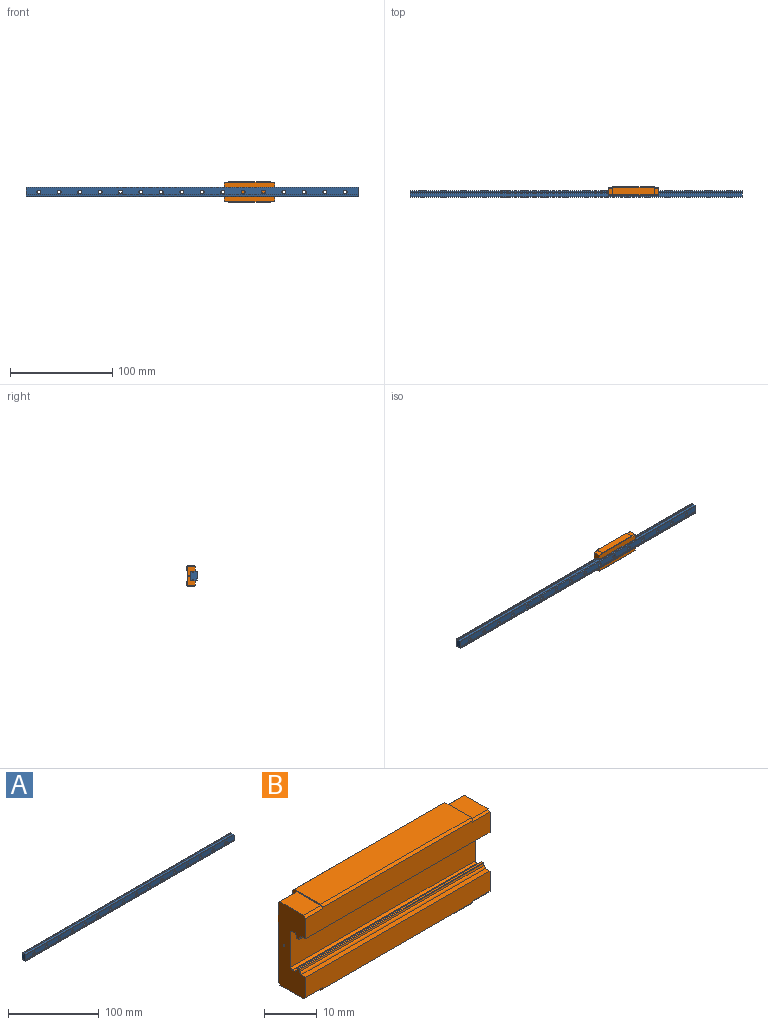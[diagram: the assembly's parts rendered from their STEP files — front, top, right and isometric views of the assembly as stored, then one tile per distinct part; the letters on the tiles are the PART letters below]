
ASSEMBLY  parts=2 mates=1
PART A: 92 faces, bbox 325x6x9 mm
  f0: cylinder r=1mm len=325mm, axis (-1,0,0), area 211.8mm2, adj f1,f25,f26,f27
  f1: plane 325x0.72mm, normal (0,0,1), area 235.4mm2, adj f0,f2,f26,f27
  f2: cylinder r=0.79mm len=325mm, axis (-1,0,0), area 217.9mm2, adj f1,f3,f26,f27
  f3: plane 325x0.45mm, normal (0,-0.98,0.18), area 148.1mm2, adj f2,f4,f26,f27
  f4: cylinder r=0.4mm len=325mm, axis (-1,0,0), area 61.9mm2, adj f3,f5,f26,f27
  f5: plane 325x0.35mm, normal (0,0,1), area 113.3mm2, adj f4,f6,f26,f27
  f6: cylinder r=0.4mm len=325mm, axis (-1,0,0), area 61.9mm2, adj f5,f7,f26,f27
  f7: plane 325x0.45mm, normal (0,0.98,0.18), area 148.1mm2, adj f6,f8,f26,f27
  f8: cylinder r=0.79mm len=325mm, axis (-1,0,0), area 217.9mm2, adj f7,f9,f26,f27
  f9: plane 325x2.72mm, normal (0,0,1), area 885.4mm2, adj f8,f10,f26,f27
  f10: plane 325x0.5mm, normal (0,-0.71,0.71), area 229.8mm2, adj f9,f11,f26,f27
  f11: plane 325x6.1mm, normal (0,-1,0), area 1791.4mm2, adj f10,f12,f26,f27,f31,f35,f39,f43
  f12: cylinder r=0.5mm len=325mm, axis (-1,0,0), area 301.4mm2, adj f11,f13,f26,f27
  f13: plane 325x1.1mm, normal (0,-1,0), area 357.5mm2, adj f12,f14,f26,f27
  f14: plane 325x0.5mm, normal (0,-0.71,-0.71), area 229.8mm2, adj f13,f15,f26,f27
  f15: plane 325x2.72mm, normal (0,0,-1), area 885.4mm2, adj f14,f16,f26,f27
  f16: cylinder r=0.79mm len=325mm, axis (-1,0,0), area 217.9mm2, adj f15,f17,f26,f27
  f17: plane 325x0.45mm, normal (0,0.98,-0.18), area 148.1mm2, adj f16,f18,f26,f27
  f18: cylinder r=0.4mm len=325mm, axis (-1,0,0), area 61.9mm2, adj f17,f19,f26,f27
  f19: plane 325x0.35mm, normal (0,0,-1), area 113.3mm2, adj f18,f20,f26,f27
  f20: cylinder r=0.4mm len=325mm, axis (-1,0,0), area 61.9mm2, adj f19,f21,f26,f27
  f21: plane 325x0.45mm, normal (0,-0.98,-0.18), area 148.1mm2, adj f20,f22,f26,f27
  f22: cylinder r=0.79mm len=325mm, axis (-1,0,0), area 217.9mm2, adj f21,f23,f26,f27
  f23: plane 325x0.72mm, normal (0,0,-1), area 235.4mm2, adj f22,f24,f26,f27
  f24: cylinder r=1mm len=325mm, axis (-1,0,0), area 211.8mm2, adj f23,f25,f26,f27
  f25: plane 325x8.2mm, normal (0,1,0), area 2212.6mm2, adj f0,f24,f26,f27,f28,f32,f36,f40
  f26: plane 9x6mm, normal (1,0,0), area 51.3mm2, adj f0,f1,f2,f3,f4,f5,f6,f7
  f27: plane 9x6mm, normal (-1,0,0), area 51.3mm2, adj f0,f1,f2,f3,f4,f5,f6,f7
  f28: cylinder r=3mm len=6mm, axis (0,-1,0), area 66mm2, adj f25,f29
  f29: plane 6x6mm, normal (0,1,0), area 18.7mm2, adj f28,f30
  f30: cylinder r=1.75mm len=3.5mm, axis (0,-1,0), area 25.3mm2, adj f29,f31
  f31: cone r=1.75mm half-angle=45deg, axis (0,-1,0), area 3.3mm2, adj f11,f30
  f32: cylinder r=3mm len=6mm, axis (0,-1,0), area 66mm2, adj f25,f33
  f33: plane 6x6mm, normal (0,1,0), area 18.7mm2, adj f32,f34
  f34: cylinder r=1.75mm len=3.5mm, axis (0,-1,0), area 25.3mm2, adj f33,f35
  f35: cone r=1.75mm half-angle=45deg, axis (0,-1,0), area 3.3mm2, adj f11,f34
  f36: cylinder r=3mm len=6mm, axis (0,-1,0), area 66mm2, adj f25,f37
  f37: plane 6x6mm, normal (0,1,0), area 18.7mm2, adj f36,f38
  f38: cylinder r=1.75mm len=3.5mm, axis (0,-1,0), area 25.3mm2, adj f37,f39
  f39: cone r=1.75mm half-angle=45deg, axis (0,-1,0), area 3.3mm2, adj f11,f38
  f40: cylinder r=3mm len=6mm, axis (0,-1,0), area 66mm2, adj f25,f41
  f41: plane 6x6mm, normal (0,1,0), area 18.7mm2, adj f40,f42
  f42: cylinder r=1.75mm len=3.5mm, axis (0,-1,0), area 25.3mm2, adj f41,f43
  f43: cone r=1.75mm half-angle=45deg, axis (0,-1,0), area 3.3mm2, adj f11,f42
  f44: cylinder r=3mm len=6mm, axis (0,-1,0), area 66mm2, adj f25,f45
  f45: plane 6x6mm, normal (0,1,0), area 18.7mm2, adj f44,f46
  f46: cylinder r=1.75mm len=3.5mm, axis (0,-1,0), area 25.3mm2, adj f45,f47
  f47: cone r=1.75mm half-angle=45deg, axis (0,-1,0), area 3.3mm2, adj f11,f46
  f48: cylinder r=3mm len=6mm, axis (0,-1,0), area 66mm2, adj f25,f49
  f49: plane 6x6mm, normal (0,1,0), area 18.7mm2, adj f48,f50
  f50: cylinder r=1.75mm len=3.5mm, axis (0,-1,0), area 25.3mm2, adj f49,f51
  f51: cone r=1.75mm half-angle=45deg, axis (0,-1,0), area 3.3mm2, adj f11,f50
  f52: cylinder r=3mm len=6mm, axis (0,-1,0), area 66mm2, adj f25,f53
  f53: plane 6x6mm, normal (0,1,0), area 18.7mm2, adj f52,f54
  f54: cylinder r=1.75mm len=3.5mm, axis (0,-1,0), area 25.3mm2, adj f53,f55
  f55: cone r=1.75mm half-angle=45deg, axis (0,-1,0), area 3.3mm2, adj f11,f54
  f56: cylinder r=3mm len=6mm, axis (0,-1,0), area 66mm2, adj f25,f57
  f57: plane 6x6mm, normal (0,1,0), area 18.7mm2, adj f56,f58
  f58: cylinder r=1.75mm len=3.5mm, axis (0,-1,0), area 25.3mm2, adj f57,f59
  f59: cone r=1.75mm half-angle=45deg, axis (0,-1,0), area 3.3mm2, adj f11,f58
  f60: cylinder r=3mm len=6mm, axis (0,-1,0), area 66mm2, adj f25,f61
  f61: plane 6x6mm, normal (0,1,0), area 18.7mm2, adj f60,f62
  f62: cylinder r=1.75mm len=3.5mm, axis (0,-1,0), area 25.3mm2, adj f61,f63
  f63: cone r=1.75mm half-angle=45deg, axis (0,-1,0), area 3.3mm2, adj f11,f62
  f64: cylinder r=3mm len=6mm, axis (0,-1,0), area 66mm2, adj f25,f65
  f65: plane 6x6mm, normal (0,1,0), area 18.7mm2, adj f64,f66
  f66: cylinder r=1.75mm len=3.5mm, axis (0,-1,0), area 25.3mm2, adj f65,f67
  f67: cone r=1.75mm half-angle=45deg, axis (0,-1,0), area 3.3mm2, adj f11,f66
  f68: cylinder r=3mm len=6mm, axis (0,-1,0), area 66mm2, adj f25,f69
  f69: plane 6x6mm, normal (0,1,0), area 18.7mm2, adj f68,f70
  f70: cylinder r=1.75mm len=3.5mm, axis (0,-1,0), area 25.3mm2, adj f69,f71
  f71: cone r=1.75mm half-angle=45deg, axis (0,-1,0), area 3.3mm2, adj f11,f70
  f72: cylinder r=3mm len=6mm, axis (0,-1,0), area 66mm2, adj f25,f73
  f73: plane 6x6mm, normal (0,1,0), area 18.7mm2, adj f72,f74
  f74: cylinder r=1.75mm len=3.5mm, axis (0,-1,0), area 25.3mm2, adj f73,f75
  f75: cone r=1.75mm half-angle=45deg, axis (0,-1,0), area 3.3mm2, adj f11,f74
  f76: cylinder r=3mm len=6mm, axis (0,-1,0), area 66mm2, adj f25,f77
  f77: plane 6x6mm, normal (0,1,0), area 18.7mm2, adj f76,f78
  f78: cylinder r=1.75mm len=3.5mm, axis (0,-1,0), area 25.3mm2, adj f77,f79
  f79: cone r=1.75mm half-angle=45deg, axis (0,-1,0), area 3.3mm2, adj f11,f78
  f80: cylinder r=3mm len=6mm, axis (0,-1,0), area 66mm2, adj f25,f81
  f81: plane 6x6mm, normal (0,1,0), area 18.7mm2, adj f80,f82
  f82: cylinder r=1.75mm len=3.5mm, axis (0,-1,0), area 25.3mm2, adj f81,f83
  f83: cone r=1.75mm half-angle=45deg, axis (0,-1,0), area 3.3mm2, adj f11,f82
  f84: cylinder r=3mm len=6mm, axis (0,-1,0), area 66mm2, adj f25,f85
  f85: plane 6x6mm, normal (0,1,0), area 18.7mm2, adj f84,f86
  f86: cylinder r=1.75mm len=3.5mm, axis (0,-1,0), area 25.3mm2, adj f85,f87
  f87: cone r=1.75mm half-angle=45deg, axis (0,-1,0), area 3.3mm2, adj f11,f86
  f88: cylinder r=3mm len=6mm, axis (0,-1,0), area 66mm2, adj f25,f89
  f89: plane 6x6mm, normal (0,1,0), area 18.7mm2, adj f88,f90
  f90: cylinder r=1.75mm len=3.5mm, axis (0,-1,0), area 25.3mm2, adj f89,f91
  f91: cone r=1.75mm half-angle=45deg, axis (0,-1,0), area 3.3mm2, adj f11,f90
PART B: 85 faces, bbox 49.6x8x20 mm
  f0: plane 40.4x2.34mm, normal (0,0,-1), area 94.5mm2, adj f6,f45,f55,f61
  f1: plane 6.01x4.22mm, normal (-1,0,0), area 4.2mm2, adj f7,f8,f9,f10,f37,f46,f47,f48
  f2: plane 6.01x4.22mm, normal (1,0,0), area 4.2mm2, adj f7,f8,f9,f10,f37,f56,f57,f58
  f3: plane 40.4x0.5mm, normal (0,0.71,0.71), area 28.6mm2, adj f4,f13,f44,f54
  f4: plane 40.4x7mm, normal (0,0,1), area 282.8mm2, adj f3,f5,f44,f54
  f5: plane 40.4x0.5mm, normal (0,-0.71,0.71), area 28.6mm2, adj f4,f14,f44,f54
  f6: plane 40.4x0.5mm, normal (0,-0.71,-0.71), area 28.6mm2, adj f0,f36,f45,f55
  f7: plane 40.4x3.34mm, normal (0,0,-1), area 134.9mm2, adj f1,f2,f8,f61
  f8: plane 40.4x0.5mm, normal (0,0.71,-0.71), area 28.6mm2, adj f1,f2,f7,f9
  f9: plane 40.4x4.5mm, normal (0,1,0), area 160.6mm2, adj f1,f2,f8,f10,f66,f72,f78
  f10: plane 40.4x0.3mm, normal (0,0.71,0.71), area 17.1mm2, adj f1,f2,f9,f37
  f11: plane 40.4x7.97mm, normal (0,1,0), area 322.1mm2, adj f12,f37,f44,f54
  f12: plane 40.4x0.3mm, normal (0,0.71,-0.71), area 17.1mm2, adj f11,f13,f44,f54
  f13: plane 40.4x4.5mm, normal (0,1,0), area 160.6mm2, adj f3,f12,f44,f54,f63,f69,f75
  f14: plane 49.6x5mm, normal (0,-1,0), area 245.2mm2, adj f5,f15,f38,f39,f41,f44,f51,f54
  f15: plane 49.6x1.22mm, normal (0,0,-1), area 60.5mm2, adj f14,f16,f38,f39
  f16: cylinder r=0.79mm len=49.6mm, axis (-1,0,0), area 33.6mm2, adj f15,f17,f38,f39
  f17: plane 49.6x0.44mm, normal (0,-0.98,-0.17), area 22.3mm2, adj f16,f18,f38,f39
  f18: cylinder r=0.4mm len=49.6mm, axis (-1,0,0), area 9.6mm2, adj f17,f19,f38,f39
  f19: plane 49.6x0.35mm, normal (0,0,-1), area 17.3mm2, adj f18,f20,f38,f39
  f20: cylinder r=0.4mm len=49.6mm, axis (-1,0,0), area 9.6mm2, adj f19,f21,f38,f39
  f21: plane 49.6x0.44mm, normal (0,0.98,-0.17), area 22.3mm2, adj f20,f22,f38,f39
  f22: cylinder r=0.79mm len=49.6mm, axis (-1,0,0), area 33.6mm2, adj f21,f23,f38,f39
  f23: plane 49.6x0.72mm, normal (0,0,-1), area 35.7mm2, adj f22,f24,f38,f39
  f24: cylinder r=1mm len=49.6mm, axis (-1,0,0), area 32.3mm2, adj f23,f25,f38,f39
  f25: plane 49.6x8.2mm, normal (0,-1,0), area 406.7mm2, adj f24,f26,f38,f39
  f26: cylinder r=1mm len=49.6mm, axis (-1,0,0), area 32.3mm2, adj f25,f27,f38,f39
  f27: plane 49.6x0.72mm, normal (0,0,1), area 35.7mm2, adj f26,f28,f38,f39
  f28: cylinder r=0.79mm len=49.6mm, axis (-1,0,0), area 33.6mm2, adj f27,f29,f38,f39
  f29: plane 49.6x0.44mm, normal (0,0.98,0.17), area 22.3mm2, adj f28,f30,f38,f39
  f30: cylinder r=0.4mm len=49.6mm, axis (-1,0,0), area 9.6mm2, adj f29,f31,f38,f39
  f31: plane 49.6x0.35mm, normal (0,0,1), area 17.3mm2, adj f30,f32,f38,f39
  f32: cylinder r=0.4mm len=49.6mm, axis (-1,0,0), area 9.6mm2, adj f31,f33,f38,f39
  f33: plane 49.6x0.44mm, normal (0,-0.98,0.17), area 22.3mm2, adj f32,f34,f38,f39
  f34: cylinder r=0.79mm len=49.6mm, axis (-1,0,0), area 33.6mm2, adj f33,f35,f38,f39
  f35: plane 49.6x1.22mm, normal (0,0,1), area 60.5mm2, adj f34,f36,f38,f39
  f36: plane 49.6x5mm, normal (0,-1,0), area 245.2mm2, adj f6,f35,f38,f39,f45,f49,f55,f59
  f37: cylinder r=1mm len=49.6mm, axis (-1,0,0), area 64.4mm2, adj f1,f2,f10,f11,f38,f39,f42,f44
  f38: plane 19.4x7.4mm, normal (1,0,0), area 109.2mm2, adj f14,f15,f16,f17,f18,f19,f20,f21
  f39: plane 19.4x7.4mm, normal (-1,0,0), area 109.2mm2, adj f14,f15,f16,f17,f18,f19,f20,f21
  f40: plane 6.4x4.6mm, normal (0,0,1), area 29.4mm2, adj f39,f41,f43,f44
  f41: plane 4.6x0.5mm, normal (0,-0.71,0.71), area 3.3mm2, adj f14,f39,f40,f44
  f42: plane 13.18x4.6mm, normal (0,1,0), area 60.6mm2, adj f37,f39,f43,f44
  f43: plane 4.6x0.5mm, normal (0,0.71,0.71), area 3.3mm2, adj f39,f40,f42,f44
  f44: plane 13.98x8mm, normal (-1,0,0), area 7.8mm2, adj f3,f4,f5,f11,f12,f13,f14,f37
  f45: plane 3.22x0.8mm, normal (-1,0,0), area 0.9mm2, adj f0,f6,f36,f48,f49,f61
  f46: plane 5.21x4.6mm, normal (0,1,0), area 24mm2, adj f1,f37,f39,f47
  f47: plane 4.6x0.5mm, normal (0,0.71,-0.71), area 3.3mm2, adj f1,f39,f46,f48
  f48: plane 6.4x4.6mm, normal (0,0,-1), area 29.4mm2, adj f1,f39,f45,f47,f49,f60
  f49: plane 4.6x0.5mm, normal (0,-0.71,-0.71), area 3.3mm2, adj f36,f39,f45,f48
  f50: plane 6.4x4.6mm, normal (0,0,1), area 29.4mm2, adj f38,f51,f53,f54
  f51: plane 4.6x0.5mm, normal (0,-0.71,0.71), area 3.3mm2, adj f14,f38,f50,f54
  f52: plane 13.18x4.6mm, normal (0,1,0), area 60.6mm2, adj f37,f38,f53,f54
  f53: plane 4.6x0.5mm, normal (0,0.71,0.71), area 3.3mm2, adj f38,f50,f52,f54
  f54: plane 13.98x8mm, normal (1,0,0), area 7.8mm2, adj f3,f4,f5,f11,f12,f13,f14,f37
  f55: plane 3.22x0.8mm, normal (1,0,0), area 0.9mm2, adj f0,f6,f36,f58,f59,f61
  f56: plane 5.21x4.6mm, normal (0,1,0), area 24mm2, adj f2,f37,f38,f57
  f57: plane 4.6x0.5mm, normal (0,0.71,-0.71), area 3.3mm2, adj f2,f38,f56,f58
  f58: plane 6.4x4.6mm, normal (0,0,-1), area 29.4mm2, adj f2,f38,f55,f57,f59,f62
  f59: plane 4.6x0.5mm, normal (0,-0.71,-0.71), area 3.3mm2, adj f36,f38,f55,f58
  f60: plane 0.56x0.05mm, normal (1,0,0), area 0mm2, adj f48,f61
  f61: cylinder r=0.8mm len=40.4mm, axis (1,0,0), area 62.9mm2, adj f0,f1,f2,f7,f45,f55,f60,f62
  f62: plane 0.56x0.05mm, normal (-1,0,0), area 0mm2, adj f58,f61
  f63: cone r=1.5mm half-angle=45deg, axis (0,1,0), area 3.3mm2, adj f13,f64
  f64: cylinder r=1.23mm len=4.02mm, axis (0,-1,0), area 31.1mm2, adj f63,f65
  f65: cone r=1.23mm half-angle=60deg, axis (0,1,0), area 5.5mm2, adj f64
  f66: cone r=1.5mm half-angle=45deg, axis (0,1,0), area 3.3mm2, adj f9,f67
  f67: cylinder r=1.23mm len=4.02mm, axis (0,-1,0), area 31.1mm2, adj f66,f68
  f68: cone r=1.23mm half-angle=60deg, axis (0,1,0), area 5.5mm2, adj f67
  f69: cone r=1.5mm half-angle=45deg, axis (0,1,0), area 3.3mm2, adj f13,f70
  f70: cylinder r=1.23mm len=4.02mm, axis (0,-1,0), area 31.1mm2, adj f69,f71
  f71: cone r=1.23mm half-angle=60deg, axis (0,1,0), area 5.5mm2, adj f70
  f72: cone r=1.5mm half-angle=45deg, axis (0,1,0), area 3.3mm2, adj f9,f73
  f73: cylinder r=1.23mm len=4.02mm, axis (0,-1,0), area 31.1mm2, adj f72,f74
  f74: cone r=1.23mm half-angle=60deg, axis (0,1,0), area 5.5mm2, adj f73
  f75: cone r=1.5mm half-angle=45deg, axis (0,1,0), area 3.3mm2, adj f13,f76
  f76: cylinder r=1.23mm len=4.02mm, axis (0,-1,0), area 31.1mm2, adj f75,f77
  f77: cone r=1.23mm half-angle=60deg, axis (0,1,0), area 5.5mm2, adj f76
  f78: cone r=1.5mm half-angle=45deg, axis (0,1,0), area 3.3mm2, adj f9,f79
  f79: cylinder r=1.23mm len=4.02mm, axis (0,-1,0), area 31.1mm2, adj f78,f80
  f80: cone r=1.23mm half-angle=60deg, axis (0,1,0), area 5.5mm2, adj f79
  f81: cylinder r=0.25mm len=4.6mm, axis (1,0,0), area 7.2mm2, adj f39,f82
  f82: plane 0.5x0.5mm, normal (-1,0,0), area 0.2mm2, adj f81
  f83: plane 0.5x0.5mm, normal (1,0,0), area 0.2mm2, adj f84
  f84: cylinder r=0.25mm len=4.6mm, axis (1,0,0), area 7.2mm2, adj f38,f83
PLACE A t=(12.18,64.51,-30.07)mm fixed
PLACE B t=(193.64,66.51,-30.07)mm
MATE slider B.f28 <-> A.f16  axis (-1,0,0) through (218.44,68.51,-34.72)mm
